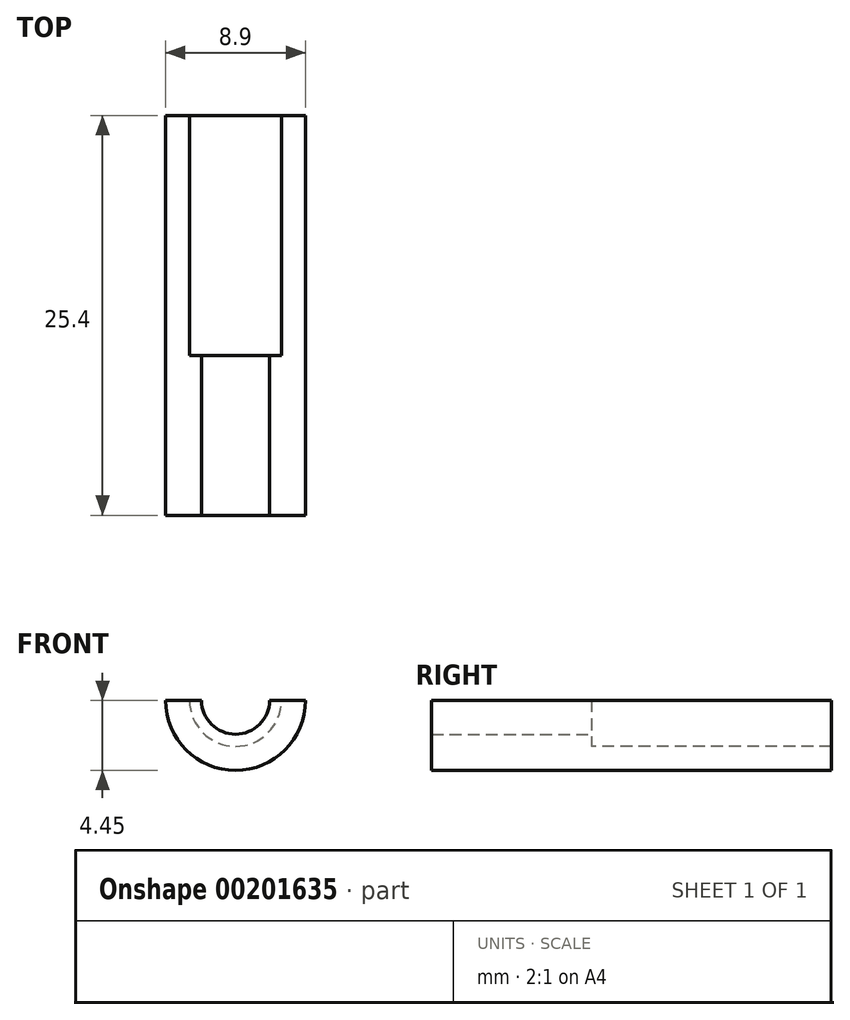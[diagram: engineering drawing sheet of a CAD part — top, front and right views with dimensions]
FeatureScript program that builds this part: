
annotation { "Feature Type Name" : "Feature", "Feature Type Description" : "" }
export const myFeature = defineFeature(function(context is Context, id is Id, definition is map)
    precondition{}
    {
        {
            var Q0;
            Q0=qCreatedBy(makeId("Front.planeOp"),FACE);
            var sketch = newSketch(context, id + "F0", { "sketchPlane" : qUnion([Q0])});
            skCircle(sketch, "E0", {"center": v(0, 0) * mm, "radius": 4.45 * mm});
            skCircle(sketch, "E1", {"center": v(0, 0) * mm, "radius": 2.16 * mm});
            skSolve(sketch);
        }
        {
            var Q0;
            Q0=qSketchRegion(id+"F0",true);
            extrude(context, id + "F1", {"entities" : qUnion([Q0]), "depth" : 10.16 * mm});
        }
        {
            var Q0;
            Q0=qCreatedBy(makeId("Front.planeOp"),FACE);
            var sketch = newSketch(context, id + "F2", { "sketchPlane" : qUnion([Q0])});
            skCircle(sketch, "E2", {"center": v(0, 0) * mm, "radius": 2.92 * mm});
            skCircle(sketch, "E3", {"center": v(0, 0) * mm, "radius": 4.45 * mm});
            skSolve(sketch);
        }
        {
            var Q0;
            Q0=qSketchRegion(id+"F2",true);
            extrude(context, id + "F3", {"entities" : qUnion([Q0]), "operationType" : NewBodyOperationType.ADD, "oppositeDirection" : true, "depth" : 15.24 * mm});
        }
        {
            var Q0;
            Q0=qCreatedBy(makeId("Front.planeOp"),FACE);
            var sketch = newSketch(context, id + "F4", { "sketchPlane" : qUnion([Q0])});
            skLineSegment(sketch, "E4.bottom", {"start": v(10.46, 8.3) * mm, "end": v(-9.73, 8.3) * mm});
            skLineSegment(sketch, "E4.top", {"start": v(10.46, 0) * mm, "end": v(-9.73, 0) * mm});
            skLineSegment(sketch, "E4.left", {"start": v(10.46, 8.3) * mm, "end": v(10.46, 0) * mm});
            skLineSegment(sketch, "E4.right", {"start": v(-9.73, 8.3) * mm, "end": v(-9.73, 0) * mm});
            skSolve(sketch);
        }
        {
            var Q0;
            Q0=makeQuery(id+"F4.imprint","IMPRINT",FACE,{"disambiguationData":[TD([[makeQuery(id+"F4.imprint","IMPRINT",EDGE,{"derivedFrom":sQuery(id+"F4.wireOp",EDGE,"E4.bottom")}),1.0]])]});
            extrude(context, id + "F5", {"entities" : qUnion([Q0]), "operationType" : NewBodyOperationType.REMOVE, "endBound" : BoundingType.THROUGH_ALL, "oppositeDirection" : true, "depth" : 25.4 * mm, "hasSecondDirection" : true, "secondDirectionBound" : SecondDirectionBoundingType.THROUGH_ALL, "secondDirectionOppositeDirection" : false, "secondDirectionDepth" : 25.4 * mm});
        }
    });
